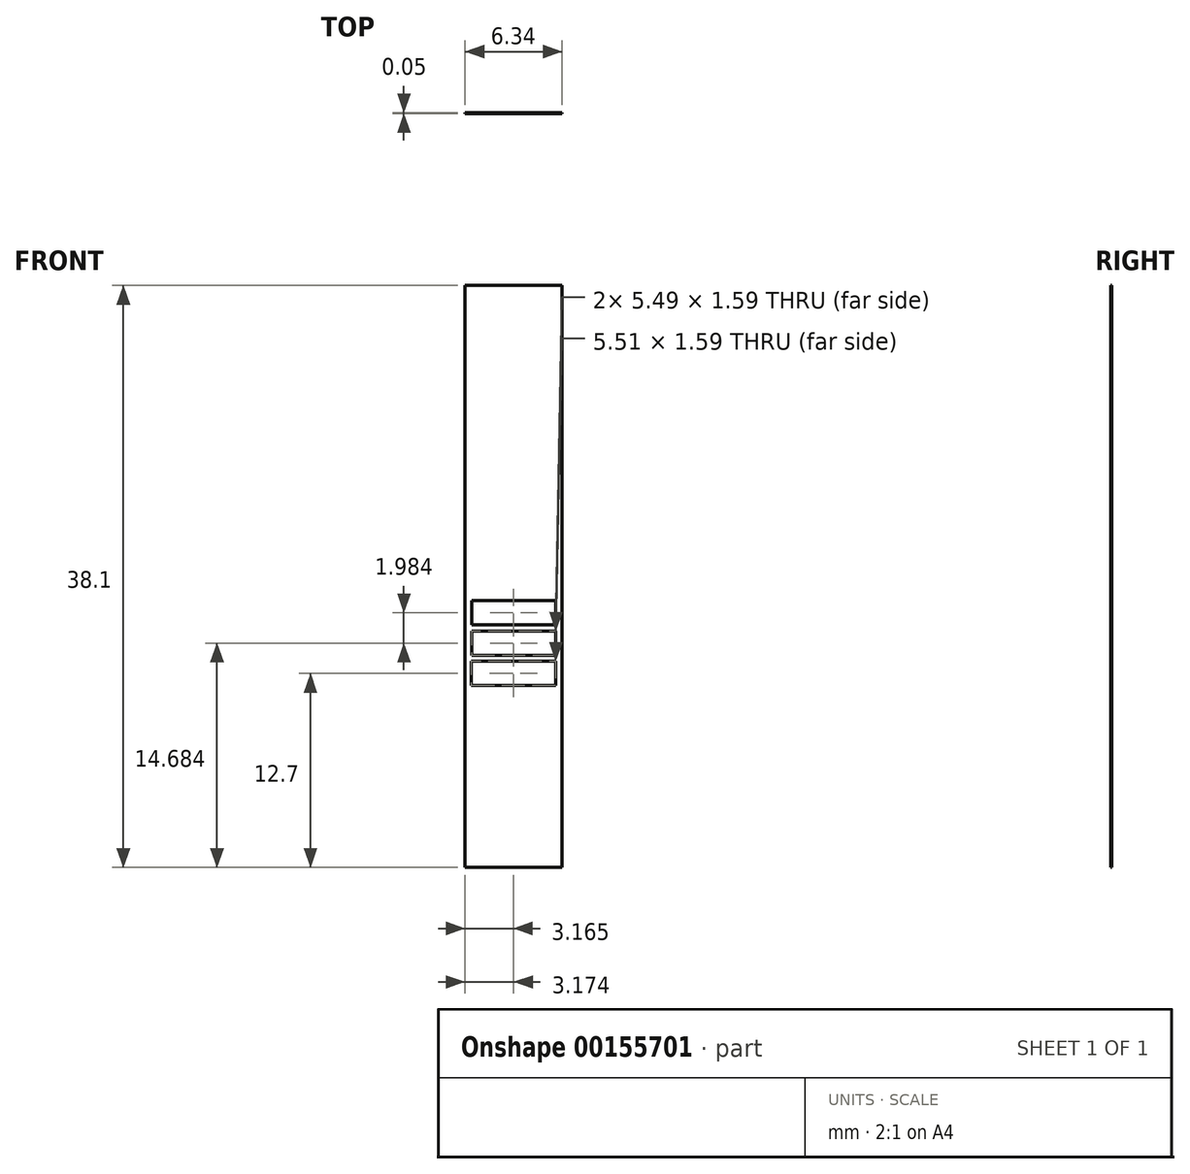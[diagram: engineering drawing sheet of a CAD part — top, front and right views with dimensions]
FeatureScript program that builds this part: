
annotation { "Feature Type Name" : "Feature", "Feature Type Description" : "" }
export const myFeature = defineFeature(function(context is Context, id is Id, definition is map)
    precondition{}
    {
        {
            var Q0;
            Q0=qCreatedBy(makeId("Front.planeOp"),FACE);
            var sketch = newSketch(context, id + "F0", { "sketchPlane" : qUnion([Q0])});
            skLineSegment(sketch, "E0.bottom", {"start": v(3.17, -19.05) * mm, "end": v(-3.18, -19.05) * mm});
            skLineSegment(sketch, "E0.top", {"start": v(3.18, 19.05) * mm, "end": v(-3.17, 19.05) * mm});
            skLineSegment(sketch, "E0.left", {"start": v(3.17, -19.05) * mm, "end": v(3.18, 19.05) * mm});
            skLineSegment(sketch, "E0.right", {"start": v(-3.18, -19.05) * mm, "end": v(-3.17, 19.05) * mm});
            skPoint(sketch, "E0.middle", {"position": v(0, 0) * mm});
            skSolve(sketch);
        }
        {
            var Q0;
            Q0=makeQuery(id+"F0.imprint","IMPRINT",FACE,{"disambiguationData":[TD([[makeQuery(id+"F0.imprint","IMPRINT",EDGE,{"derivedFrom":sQuery(id+"F0.wireOp",EDGE,"E0.bottom")}),-1.0]])]});
            extrude(context, id + "F1", {"entities" : qUnion([Q0]), "depth" : 5 / 101.6 * mm});
        }
        {
            var Q0;
            Q0=qCreatedBy(makeId("Front.planeOp"),FACE);
            var sketch = newSketch(context, id + "F2", { "sketchPlane" : qUnion([Q0])});
            skLineSegment(sketch, "E1.bottom", {"start": v(-2.74, -1.59) * mm, "end": v(2.75, -1.59) * mm});
            skLineSegment(sketch, "E1.top", {"start": v(-2.74, -3.18) * mm, "end": v(2.75, -3.18) * mm});
            skLineSegment(sketch, "E1.left", {"start": v(-2.74, -1.59) * mm, "end": v(-2.74, -3.18) * mm});
            skLineSegment(sketch, "E1.right", {"start": v(2.75, -1.59) * mm, "end": v(2.75, -3.18) * mm});
            skLineSegment(sketch, "E2.bottom", {"start": v(-2.74, -3.57) * mm, "end": v(2.75, -3.57) * mm});
            skLineSegment(sketch, "E2.top", {"start": v(-2.74, -5.16) * mm, "end": v(2.75, -5.16) * mm});
            skLineSegment(sketch, "E2.left", {"start": v(-2.74, -3.57) * mm, "end": v(-2.74, -5.16) * mm});
            skLineSegment(sketch, "E2.right", {"start": v(2.75, -3.57) * mm, "end": v(2.75, -5.16) * mm});
            skLineSegment(sketch, "E3.bottom", {"start": v(-2.76, -5.56) * mm, "end": v(2.75, -5.56) * mm});
            skLineSegment(sketch, "E3.top", {"start": v(-2.76, -7.14) * mm, "end": v(2.75, -7.14) * mm});
            skLineSegment(sketch, "E3.left", {"start": v(-2.76, -5.56) * mm, "end": v(-2.76, -7.14) * mm});
            skLineSegment(sketch, "E3.right", {"start": v(2.75, -5.56) * mm, "end": v(2.75, -7.14) * mm});
            skSolve(sketch);
        }
        {
            var Q0;
            Q0 = qSketchRegion(id + "F2", true);
            extrude(context, id + "F3", {"entities" : qUnion([Q0]), "operationType" : NewBodyOperationType.REMOVE, "depth" : 0.4 * mm});
        }
    });
